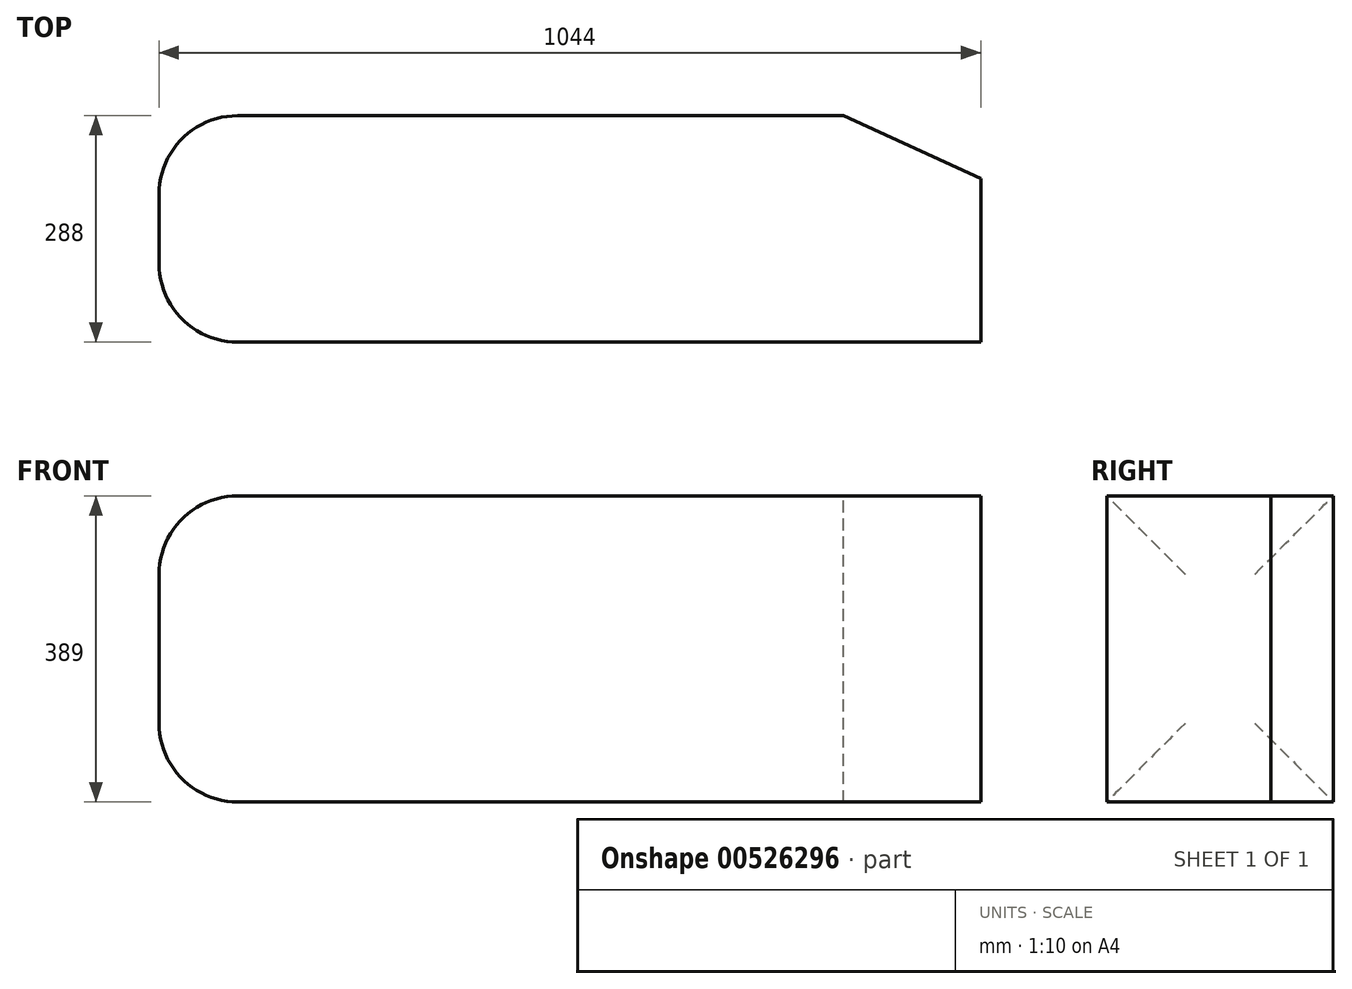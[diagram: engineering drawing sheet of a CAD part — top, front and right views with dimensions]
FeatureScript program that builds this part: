
annotation { "Feature Type Name" : "Feature", "Feature Type Description" : "" }
export const myFeature = defineFeature(function(context is Context, id is Id, definition is map)
    precondition{}
    {
        {
            var Q0;
            Q0=qCreatedBy(makeId("Front.planeOp"),FACE);
            var sketch = newSketch(context, id + "F0", { "sketchPlane" : qUnion([Q0])});
            skLineSegment(sketch, "E0.bottom", {"start": v(-525.52, 194.5) * mm, "end": v(518.48, 194.5) * mm});
            skLineSegment(sketch, "E0.top", {"start": v(-525.52, -194.5) * mm, "end": v(518.48, -194.5) * mm});
            skLineSegment(sketch, "E0.left", {"start": v(-525.52, 194.5) * mm, "end": v(-525.52, -194.5) * mm});
            skLineSegment(sketch, "E0.right", {"start": v(518.48, 194.5) * mm, "end": v(518.48, -194.5) * mm});
            skSolve(sketch);
        }
        {
            var Q0;
            Q0 = qSketchRegion(id + "F0", true);
            extrude(context, id + "F1", {"entities" : qUnion([Q0]), "oppositeDirection" : true, "depth" : 288 * mm, "offsetDistance" : 25 * mm});
        }
        {
            var Q0;
            Q0=makeQuery(id+"F1.opExtrude","SWEPT_FACE",FACE,{"disambiguationData":[OSD([sQuery(id+"F0.wireOp",EDGE,"E0.left")])]});
            fillet(context, id + "F2", {"entities" : qUnion([Q0]), "radius" : 100 * mm, "tangentPropagation" : true, "allowEdgeOverflow" : false});
        }
        {
            var Q0;
            Q0=makeQuery(id+"F1.opExtrude","SWEPT_FACE",FACE,{"disambiguationData":[OSD([sQuery(id+"F0.wireOp",EDGE,"E0.bottom")])]});
            var sketch = newSketch(context, id + "F3", { "sketchPlane" : qUnion([Q0])});
            skLineSegment(sketch, "E1", {"start": v(343.82, 288) * mm, "end": v(518.48, 208.21) * mm});
            skLineSegment(sketch, "E2", {"start": v(518.48, 208.21) * mm, "end": v(518.48, 288) * mm});
            skLineSegment(sketch, "E3", {"start": v(518.48, 288) * mm, "end": v(343.82, 288) * mm});
            skSolve(sketch);
        }
        {
            var Q0;
            Q0=makeQuery(id+"F3.imprint","IMPRINT",FACE,{"disambiguationData":[TD([[makeQuery(id+"F3.imprint","IMPRINT",EDGE,{"derivedFrom":sQuery(id+"F3.wireOp",EDGE,"E1")}),1.0]])]});
            extrude(context, id + "F4", {"entities" : qUnion([Q0]), "endBound" : BoundingType.UP_TO_NEXT, "oppositeDirection" : true, "depth" : 25 * mm, "offsetDistance" : 25 * mm});
        }
        {
            var Q0;
            Q0=makeQuery(id+"F4.opExtrude","SWEPT_BODY",BODY,{"disambiguationData":[OSD([sQuery(id+"F3.wireOp",EDGE,"E1"),sQuery(id+"F3.wireOp",EDGE,"E2"),sQuery(id+"F3.wireOp",EDGE,"E3")])]});
            var Q1;
            Q1=makeQuery(id+"F1.opExtrude","SWEPT_BODY",BODY,{"disambiguationData":[OSD([sQuery(id+"F0.wireOp",EDGE,"E0.bottom"),sQuery(id+"F0.wireOp",EDGE,"E0.top"),sQuery(id+"F0.wireOp",EDGE,"E0.left"),sQuery(id+"F0.wireOp",EDGE,"E0.right")])]});
            booleanBodies(context, id + "F5", {"operationType" : BooleanOperationType.SUBTRACTION, "tools" : qUnion([Q0]), "targets" : qUnion([Q1])});
        }
        {
            var Q0;
            Q0=makeQuery(id+"F1.opExtrude","CAP_FACE",FACE,{"disambiguationData":[OSD([sQuery(id+"F0.wireOp",EDGE,"E0.bottom"),sQuery(id+"F0.wireOp",EDGE,"E0.top"),sQuery(id+"F0.wireOp",EDGE,"E0.left"),sQuery(id+"F0.wireOp",EDGE,"E0.right")])],"isStart":true});
            var sketch = newSketch(context, id + "F6", { "sketchPlane" : qUnion([Q0])});
            skCircle(sketch, "E4", {"center": v(-324.52, 163.5) * mm, "radius": 15 * mm});
            skCircle(sketch, "E5", {"center": v(146.48, 163.5) * mm, "radius": 15 * mm});
            skLineSegment(sketch, "E6", {"start": v(-425.52, 0) * mm, "end": v(518.48, 0) * mm, "construction": true});
            skCircle(sketch, "E7.MirrorC", {"center": v(-324.52, -163.5) * mm, "radius": 15 * mm});
            skCircle(sketch, "E8.MirrorC", {"center": v(146.48, -163.5) * mm, "radius": 15 * mm});
            skSolve(sketch);
        }
        {
            var Q0;
            Q0=sQuery(id+"F6.wireOp",EDGE,"E5");
            var Q1;
            Q1=sQuery(id+"F6.wireOp",EDGE,"E8.MirrorC");
            var Q2;
            Q2=sQuery(id+"F6.wireOp",EDGE,"E4");
            var Q3;
            Q3=sQuery(id+"F6.wireOp",EDGE,"E7.MirrorC");
            extrude(context, id + "F7", {"bodyType" : ToolBodyType.SURFACE, "surfaceEntities" : qUnion([Q0, Q1, Q2, Q3]), "depth" : 50 * mm, "offsetDistance" : 25 * mm});
        }
        {
            var Q0;
            Q0=makeQuery(id+"F1.opExtrude","SWEPT_BODY",BODY,{"disambiguationData":[OSD([sQuery(id+"F0.wireOp",EDGE,"E0.bottom"),sQuery(id+"F0.wireOp",EDGE,"E0.top"),sQuery(id+"F0.wireOp",EDGE,"E0.left"),sQuery(id+"F0.wireOp",EDGE,"E0.right")])]});
            var Q1;
            Q1=makeQuery(id+"F7.opExtrude","SWEPT_BODY",BODY,{"disambiguationData":[OSD([sQuery(id+"F6.wireOp",EDGE,"E5")])]});
            var Q2;
            Q2=makeQuery(id+"F7.opExtrude","SWEPT_BODY",BODY,{"disambiguationData":[OSD([sQuery(id+"F6.wireOp",EDGE,"E4")])]});
            var Q3;
            Q3=makeQuery(id+"F7.opExtrude","SWEPT_BODY",BODY,{"disambiguationData":[OSD([sQuery(id+"F6.wireOp",EDGE,"E7.MirrorC")])]});
            var Q4;
            Q4=makeQuery(id+"F7.opExtrude","SWEPT_BODY",BODY,{"disambiguationData":[OSD([sQuery(id+"F6.wireOp",EDGE,"E8.MirrorC")])]});
            transform(context, id + "F8", {"entities" : qUnion([Q0, Q1, Q2, Q3, Q4]), "transformType" : TransformType.TRANSLATION_3D, "dx" : 0 * mm, "dy" : 50 * mm, "dz" : 0 * mm, "makeCopy" : false});
        }
    });
